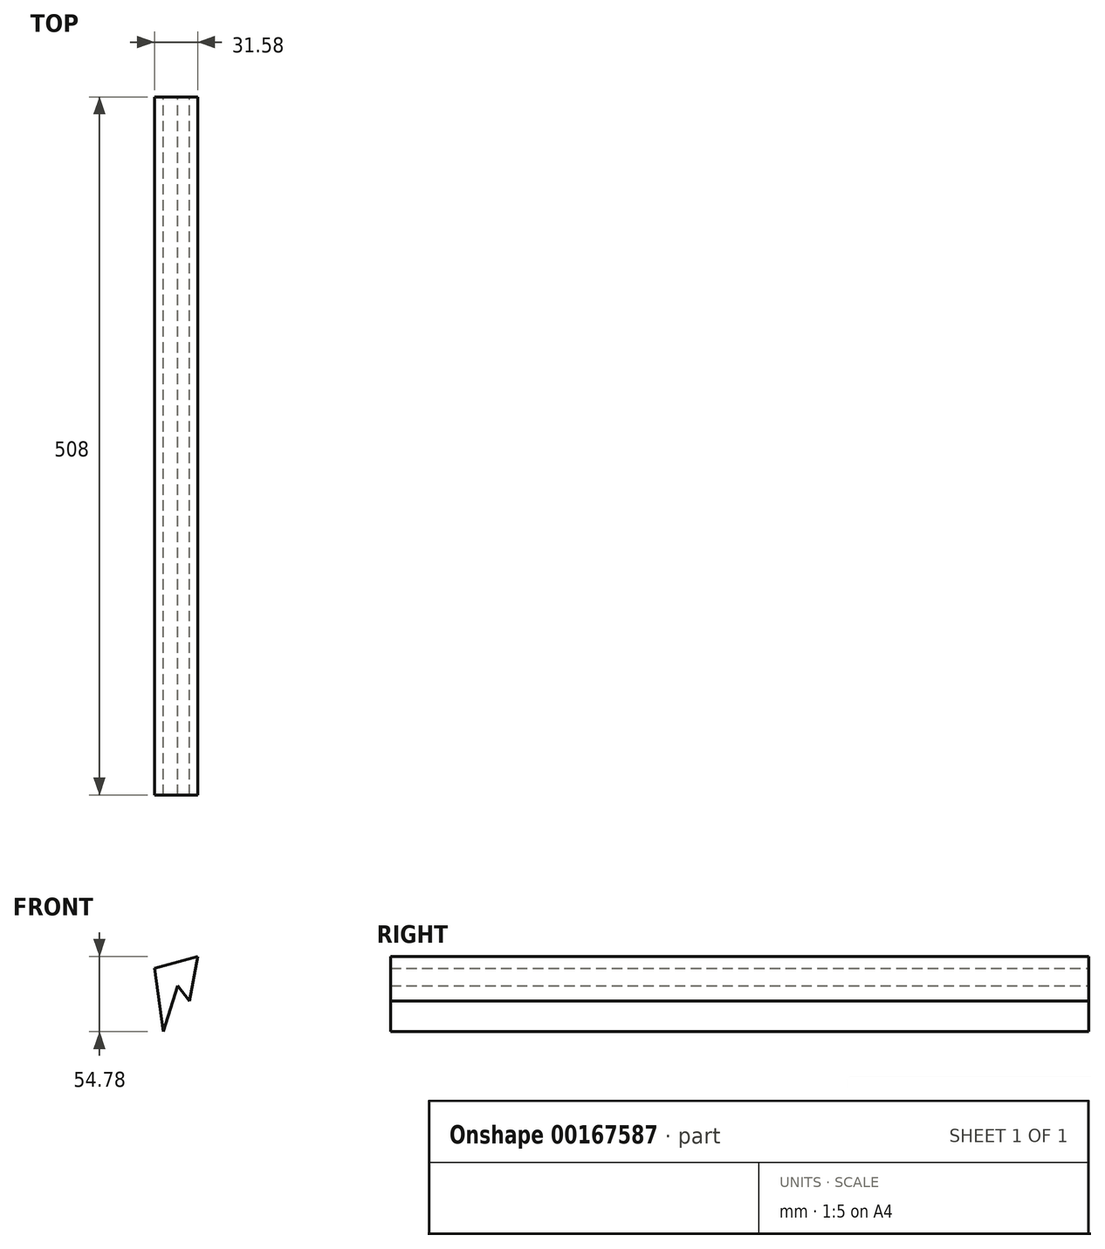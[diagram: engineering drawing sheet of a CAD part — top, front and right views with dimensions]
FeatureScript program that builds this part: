
annotation { "Feature Type Name" : "Feature", "Feature Type Description" : "" }
export const myFeature = defineFeature(function(context is Context, id is Id, definition is map)
    precondition{}
    {
        {
            var Q0;
            Q0=qCreatedBy(makeId("Front.planeOp"),FACE);
            var sketch = newSketch(context, id + "F0", { "sketchPlane" : qUnion([Q0])});
            skLineSegment(sketch, "E0", {"start": v(-10.42, -33.45) * mm, "end": v(-16.93, 12.86) * mm});
            skLineSegment(sketch, "E1", {"start": v(-16.93, 12.86) * mm, "end": v(14.65, 21.33) * mm});
            skLineSegment(sketch, "E2", {"start": v(14.65, 21.33) * mm, "end": v(8.47, -11.07) * mm});
            skLineSegment(sketch, "E3", {"start": v(8.47, -11.07) * mm, "end": v(0, 0) * mm});
            skLineSegment(sketch, "E4", {"start": v(0, 0) * mm, "end": v(-10.42, -33.45) * mm});
            skSolve(sketch);
        }
        {
            var Q0;
            Q0 = qSketchRegion(id + "F0", true);
            extrude(context, id + "F1", {"entities" : qUnion([Q0]), "depth" : 508 * mm});
        }
    });
